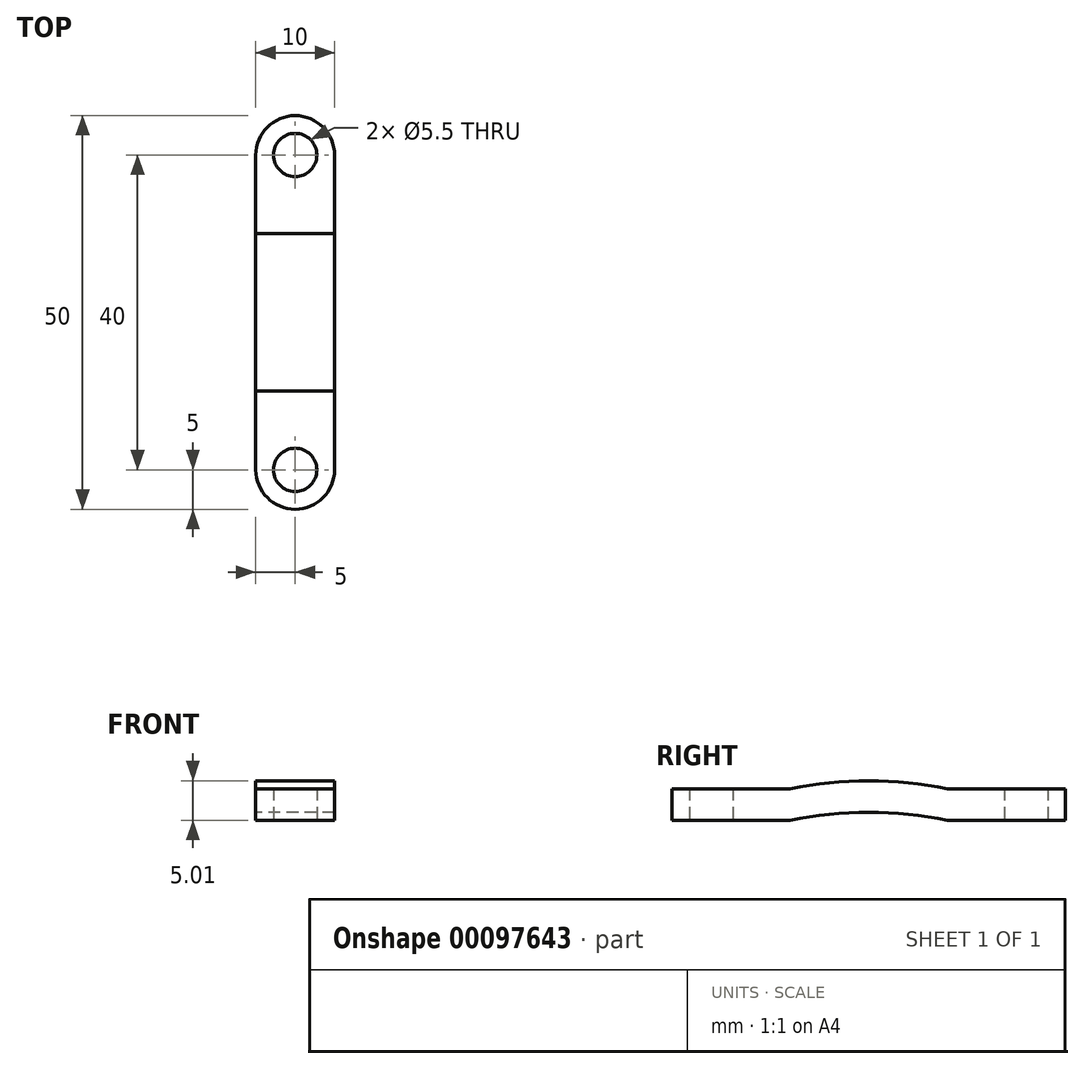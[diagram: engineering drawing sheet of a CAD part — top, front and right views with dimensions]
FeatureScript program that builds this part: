
annotation { "Feature Type Name" : "Feature", "Feature Type Description" : "" }
export const myFeature = defineFeature(function(context is Context, id is Id, definition is map)
    precondition{}
    {
        {
            var Q0;
            Q0=qCreatedBy(makeId("Top.planeOp"),FACE);
            var sketch = newSketch(context, id + "F0", { "sketchPlane" : qUnion([Q0])});
            skArc(sketch, "E0", {"start": v(-5, 0) * mm, "mid": v(0, -5) * mm, "end": v(5, 0) * mm});
            skLineSegment(sketch, "E1.top", {"start": v(5, 5) * mm, "end": v(-5, 5) * mm});
            skLineSegment(sketch, "E1.left", {"start": v(5, 0) * mm, "end": v(5, 5) * mm});
            skLineSegment(sketch, "E1.right", {"start": v(-5, 0) * mm, "end": v(-5, 5) * mm});
            skSolve(sketch);
        }
        {
            var Q0;
            Q0=makeQuery(id+"F0.imprint","IMPRINT",FACE,{"disambiguationData":[TD([[makeQuery(id+"F0.imprint","IMPRINT",EDGE,{"derivedFrom":sQuery(id+"F0.wireOp",EDGE,"E0")}),1.0]])]});
            extrude(context, id + "F1", {"entities" : qUnion([Q0]), "depth" : 4 * mm});
        }
        {
            var Q0;
            Q0=sQuery(id+"F0.wireOp",VERTEX,"E0.center");
            var Q1;
            Q1=makeQuery(id+"F1.opExtrude","SWEPT_BODY",BODY,{"disambiguationData":[OSD([sQuery(id+"F0.wireOp",EDGE,"E0"),sQuery(id+"F0.wireOp",EDGE,"E1.top"),sQuery(id+"F0.wireOp",EDGE,"E1.left"),sQuery(id+"F0.wireOp",EDGE,"E1.right")])]});
            hole(context, id + "F2", {"style" : HoleStyle.SIMPLE, "endStyle" : HoleEndStyle.BLIND, "oppositeDirection" : true, "standardTappedOrClearance" : lookupTablePath({ "standard" : "ISO", "fit" : "Normal", "size" : "M5", "type" : "Clearance" }), "standardBlindInLast" : lookupTablePath({ "fit" : "Standard", "standard" : "ISO", "size" : "M5", "type" : "Clearance" }), "holeDiameter" : 5.5 * mm, "holeDepth" : 7 * mm, "locations" : qUnion([Q0]), "scope" : qUnion([Q1])});
        }
        {
            var Q0;
            Q0=qCreatedBy(makeId("Right.planeOp"),FACE);
            var sketch = newSketch(context, id + "F3", { "sketchPlane" : qUnion([Q0])});
            skLineSegment(sketch, "E2.bottom", {"start": v(5, 0) * mm, "end": v(10, 0) * mm});
            skLineSegment(sketch, "E2.top", {"start": v(5, 4) * mm, "end": v(10, 4) * mm});
            skLineSegment(sketch, "E2.left", {"start": v(5, 0) * mm, "end": v(5, 4) * mm});
            skLineSegment(sketch, "E2.right", {"start": v(10, 0) * mm, "end": v(10, 4) * mm});
            skArc(sketch, "E3", {"start": v(30, 4) * mm, "mid": v(20, 5.01) * mm, "end": v(10, 4) * mm});
            skArc(sketch, "E4", {"start": v(30, 0) * mm, "mid": v(20, 1.01) * mm, "end": v(10, 0) * mm});
            skLineSegment(sketch, "E5.bottom", {"start": v(30, 4) * mm, "end": v(35, 4) * mm});
            skLineSegment(sketch, "E5.top", {"start": v(30, 0) * mm, "end": v(35, 0) * mm});
            skLineSegment(sketch, "E5.left", {"start": v(30, 4) * mm, "end": v(30, 0) * mm});
            skLineSegment(sketch, "E5.right", {"start": v(35, 4) * mm, "end": v(35, 0) * mm});
            skLineSegment(sketch, "E6", {"start": v(20, 5.01) * mm, "end": v(20, 1.01) * mm});
            skSolve(sketch);
        }
        {
            var Q0;
            Q0=makeQuery(id+"F3.imprint","IMPRINT",FACE,{"disambiguationData":[TD([[makeQuery(id+"F3.imprint","IMPRINT",EDGE,{"derivedFrom":sQuery(id+"F3.wireOp",EDGE,"E2.bottom")}),1.0]])]});
            var Q1;
            Q1=makeQuery(id+"F3.imprint","IMPRINT",FACE,{"disambiguationData":[TD([[makeQuery(id+"F3.imprint","IMPRINT",EDGE,{"derivedFrom":sQuery(id+"F3.wireOp",EDGE,"E2.right")}),-1.0]])]});
            var Q2;
            {var subQ0=sQuery(id+"F3.wireOp",EDGE,"E5.left");Q2=makeQuery(id+"F3.imprint","IMPRINT",FACE,{"disambiguationData":[TD([[makeQuery(id+"F3.imprint","IMPRINT",EDGE,{"derivedFrom":subQ0}),-1.0]])]});}
            var Q3;
            Q3=makeQuery(id+"F3.imprint","IMPRINT",FACE,{"disambiguationData":[TD([[makeQuery(id+"F3.imprint","IMPRINT",EDGE,{"derivedFrom":sQuery(id+"F3.wireOp",EDGE,"E5.bottom")}),-1.0]])]});
            extrude(context, id + "F4", {"entities" : qUnion([Q0, Q1, Q2, Q3]), "operationType" : NewBodyOperationType.ADD, "endBound" : BoundingType.SYMMETRIC, "depth" : 10 * mm});
        }
        {
            var Q0;
            Q0=qCreatedBy(makeId("Top.planeOp"),FACE);
            var sketch = newSketch(context, id + "F5", { "sketchPlane" : qUnion([Q0])});
            skArc(sketch, "E7", {"start": v(5, 40) * mm, "mid": v(0, 45) * mm, "end": v(-5, 40) * mm});
            skLineSegment(sketch, "E8.bottom", {"start": v(-5, 35) * mm, "end": v(5, 35) * mm});
            skLineSegment(sketch, "E8.left", {"start": v(-5, 35) * mm, "end": v(-5, 40) * mm});
            skLineSegment(sketch, "E8.right", {"start": v(5, 35) * mm, "end": v(5, 40) * mm});
            skSolve(sketch);
        }
        {
            var Q0;
            Q0=makeQuery(id+"F5.imprint","IMPRINT",FACE,{"disambiguationData":[TD([[makeQuery(id+"F5.imprint","IMPRINT",EDGE,{"derivedFrom":sQuery(id+"F5.wireOp",EDGE,"E7")}),1.0]])]});
            extrude(context, id + "F6", {"entities" : qUnion([Q0]), "operationType" : NewBodyOperationType.ADD, "depth" : 4 * mm});
        }
        {
            var Q0;
            Q0=sQuery(id+"F5.wireOp",VERTEX,"E7.center");
            var Q1;
            Q1=makeQuery(id+"F1.opExtrude","SWEPT_BODY",BODY,{"disambiguationData":[OSD([sQuery(id+"F0.wireOp",EDGE,"E0"),sQuery(id+"F0.wireOp",EDGE,"E1.top"),sQuery(id+"F0.wireOp",EDGE,"E1.left"),sQuery(id+"F0.wireOp",EDGE,"E1.right")])]});
            hole(context, id + "F7", {"style" : HoleStyle.SIMPLE, "endStyle" : HoleEndStyle.BLIND, "oppositeDirection" : true, "standardTappedOrClearance" : lookupTablePath({ "standard" : "ISO", "fit" : "Normal", "size" : "M5", "type" : "Clearance" }), "standardBlindInLast" : lookupTablePath({ "fit" : "Standard", "standard" : "ISO", "size" : "M5", "type" : "Clearance" }), "holeDiameter" : 5.5 * mm, "holeDepth" : 7 * mm, "locations" : qUnion([Q0]), "scope" : qUnion([Q1])});
        }
    });
